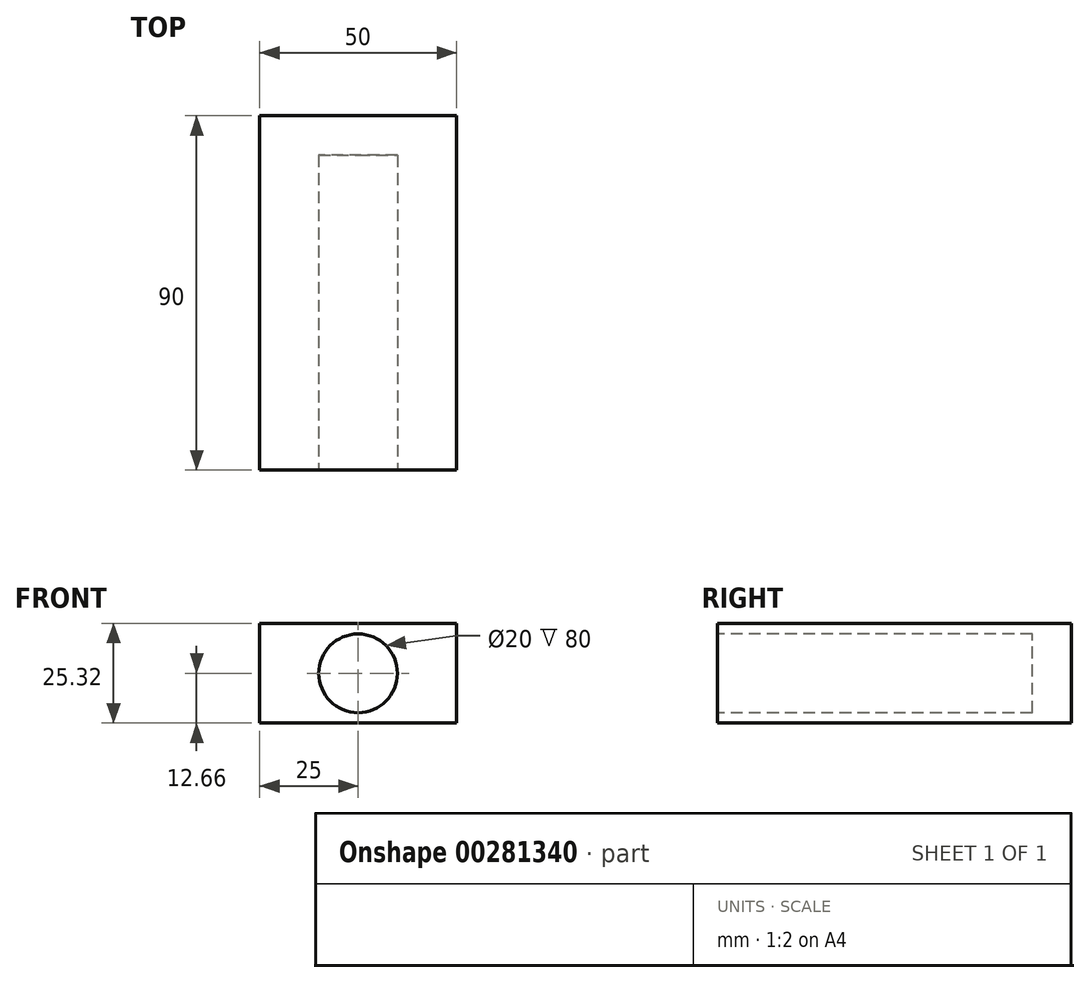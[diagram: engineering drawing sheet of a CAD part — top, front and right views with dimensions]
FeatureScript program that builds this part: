
annotation { "Feature Type Name" : "Feature", "Feature Type Description" : "" }
export const myFeature = defineFeature(function(context is Context, id is Id, definition is map)
    precondition{}
    {
        {
            var Q0;
            Q0=qCreatedBy(makeId("Front.planeOp"),FACE);
            var sketch = newSketch(context, id + "F0", { "sketchPlane" : qUnion([Q0])});
            skLineSegment(sketch, "E0.bottom", {"start": v(25, 12.66) * mm, "end": v(-25, 12.66) * mm});
            skLineSegment(sketch, "E0.top", {"start": v(25, -12.66) * mm, "end": v(-25, -12.66) * mm});
            skLineSegment(sketch, "E0.left", {"start": v(25, 12.66) * mm, "end": v(25, -12.66) * mm});
            skLineSegment(sketch, "E0.right", {"start": v(-25, 12.66) * mm, "end": v(-25, -12.66) * mm});
            skPoint(sketch, "E0.middle", {"position": v(0, 0) * mm});
            skSolve(sketch);
        }
        {
            var Q0;
            Q0 = qSketchRegion(id + "F0", true);
            extrude(context, id + "F1", {"entities" : qUnion([Q0]), "depth" : 90 * mm});
        }
        {
            var Q0;
            Q0=makeQuery(id+"F1.opExtrude","CAP_FACE",FACE,{"disambiguationData":[OSD([sQuery(id+"F0.wireOp",EDGE,"E0.bottom"),sQuery(id+"F0.wireOp",EDGE,"E0.top"),sQuery(id+"F0.wireOp",EDGE,"E0.left"),sQuery(id+"F0.wireOp",EDGE,"E0.right")])],"isStart":false});
            var sketch = newSketch(context, id + "F2", { "sketchPlane" : qUnion([Q0])});
            skCircle(sketch, "E1", {"center": v(0, 0) * mm, "radius": 10 * mm});
            skSolve(sketch);
        }
        {
            var Q0;
            Q0=makeQuery(id+"F2.imprint","IMPRINT",FACE,{"disambiguationData":[TD([[makeQuery(id+"F2.imprint","IMPRINT",EDGE,{"derivedFrom":sQuery(id+"F2.wireOp",EDGE,"E1")}),1.0]])]});
            var Q1;
            Q1=sQuery(id+"F2.wireOp",EDGE,"E1");
            extrude(context, id + "F3", {"entities" : qUnion([Q0]), "operationType" : NewBodyOperationType.REMOVE, "surfaceEntities" : qUnion([Q1]), "oppositeDirection" : true, "depth" : 80 * mm});
        }
    });
